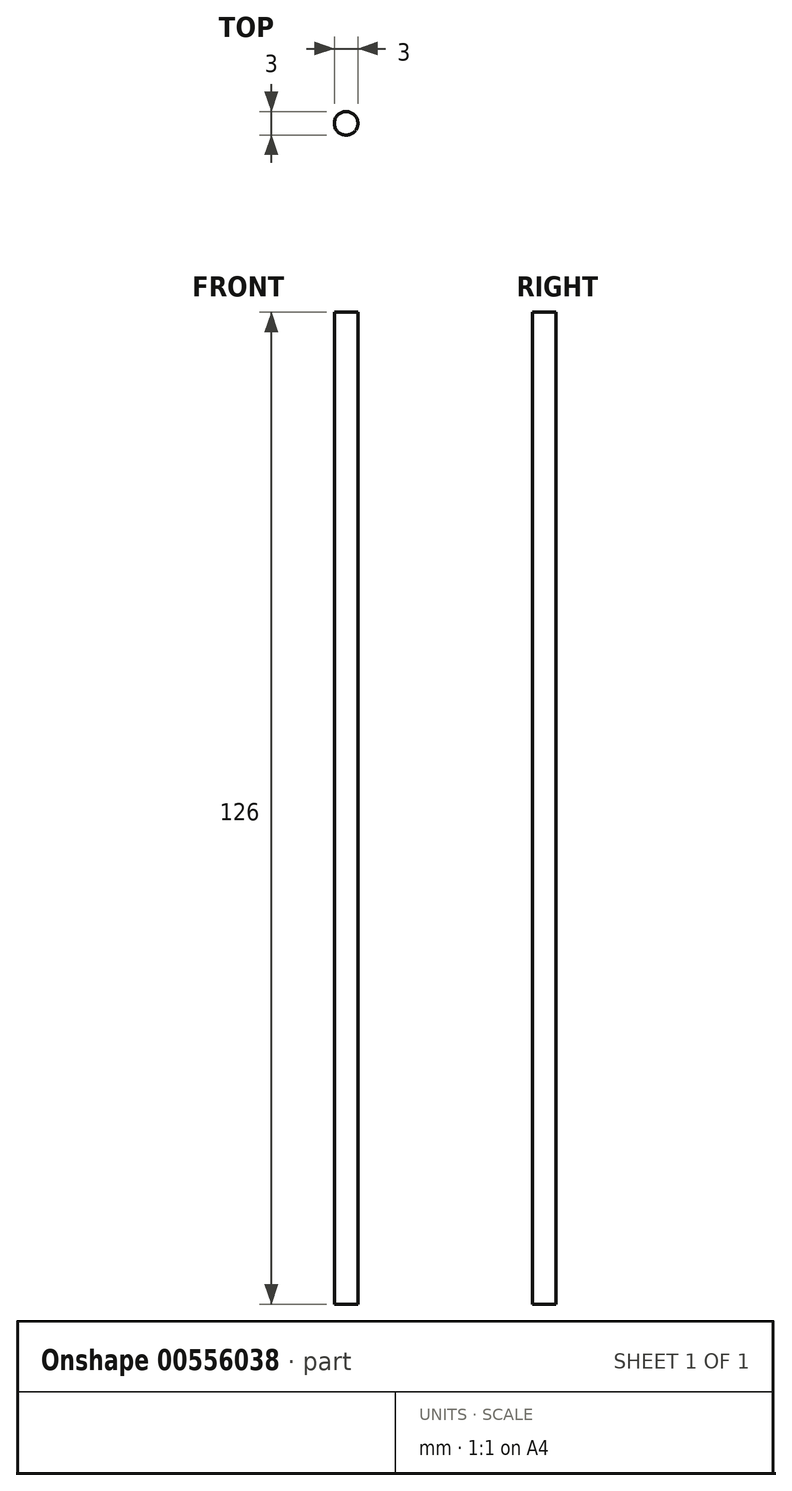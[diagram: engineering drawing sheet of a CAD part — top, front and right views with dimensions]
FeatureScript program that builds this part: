
annotation { "Feature Type Name" : "Feature", "Feature Type Description" : "" }
export const myFeature = defineFeature(function(context is Context, id is Id, definition is map)
    precondition{}
    {
        {
            var Q0;
            Q0=qCreatedBy(makeId("Top.planeOp"),FACE);
            var sketch = newSketch(context, id + "F0", { "sketchPlane" : qUnion([Q0])});
            skCircle(sketch, "E0", {"center": v(-0.8, -1.6) * mm, "radius": 1.5 * mm});
            skSolve(sketch);
        }
        {
            var Q0;
            Q0=makeQuery(id+"F0.imprint","IMPRINT",FACE,{"disambiguationData":[TD([[makeQuery(id+"F0.imprint","IMPRINT",EDGE,{"derivedFrom":sQuery(id+"F0.wireOp",EDGE,"E0")}),1.0]])]});
            extrude(context, id + "F1", {"entities" : qUnion([Q0]), "depth" : 126 * mm, "offsetDistance" : 25 * mm});
        }
    });
